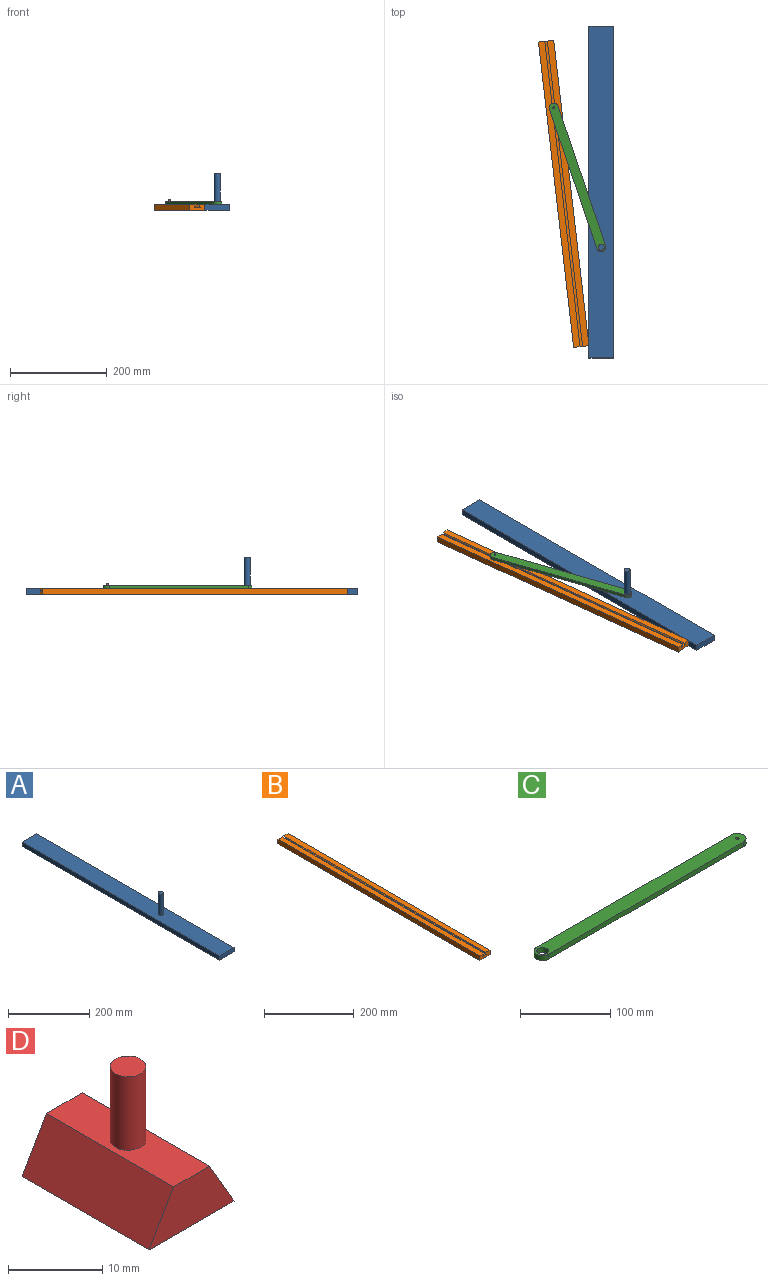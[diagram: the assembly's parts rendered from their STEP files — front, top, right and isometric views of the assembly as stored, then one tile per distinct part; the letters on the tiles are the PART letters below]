
ASSEMBLY  parts=4 mates=3
PART A: 8 faces, bbox 50.8x685.8x76.2 mm
  f0: plane 685.8x12.7mm, normal (-1,0,0), area 8709.7mm2, adj f1,f3,f4,f5
  f1: plane 685.8x50.8mm, normal (0,0,1), area 34712mm2, adj f0,f2,f4,f5,f6
  f2: plane 685.8x12.7mm, normal (1,0,0), area 8709.7mm2, adj f1,f3,f4,f5
  f3: plane 685.8x50.8mm, normal (0,0,-1), area 34838.6mm2, adj f0,f2,f4,f5
  f4: plane 50.8x12.7mm, normal (0,1,0), area 645.2mm2, adj f0,f1,f2,f3
  f5: plane 50.8x12.7mm, normal (0,-1,0), area 645.2mm2, adj f0,f1,f2,f3
  f6: cylinder r=6.35mm len=63.5mm, axis (0,0,-1), area 2533.5mm2, adj f1,f7
  f7: plane 12.7x12.7mm, normal (0,0,1), area 126.7mm2, adj f6
PART B: 10 faces, bbox 31.8x635x12.7 mm
  f0: plane 635x13.19mm, normal (0,0,1), area 8376.4mm2, adj f1,f2,f4,f8
  f1: plane 31.75x12.7mm, normal (0,1,0), area 345.9mm2, adj f0,f3,f4,f5,f6,f7,f8,f9
  f2: plane 31.75x12.7mm, normal (0,-1,0), area 345.9mm2, adj f0,f3,f4,f5,f6,f7,f8,f9
  f3: plane 635x31.75mm, normal (0,0,-1), area 20161.3mm2, adj f1,f2,f4,f6
  f4: plane 635x12.7mm, normal (1,0,0), area 8064.5mm2, adj f0,f1,f2,f3
  f5: plane 635x13.19mm, normal (0,0,1), area 8376.4mm2, adj f1,f2,f6,f7
  f6: plane 635x12.7mm, normal (-1,0,0), area 8064.5mm2, adj f1,f2,f3,f5
  f7: plane 635x6.35mm, normal (0.87,0,-0.5), area 4656mm2, adj f1,f2,f5,f9
  f8: plane 635x6.35mm, normal (-0.87,0,-0.5), area 4656mm2, adj f0,f1,f2,f9
  f9: plane 635x12.7mm, normal (0,0,1), area 8064.5mm2, adj f1,f2,f7,f8
PART C: 8 faces, bbox 323.9x19.1x6.4 mm
  f0: plane 304.8x6.35mm, normal (0,1,0), area 1935.5mm2, adj f1,f4,f6,f7
  f1: cylinder r=9.53mm len=19.05mm, axis (0,0,-1), area 190mm2, adj f0,f2,f6,f7
  f2: plane 304.8x6.35mm, normal (0,-1,0), area 1935.5mm2, adj f1,f4,f6,f7
  f3: cylinder r=6.35mm len=12.7mm, axis (0,0,-1), area 253.4mm2, adj f6,f7
  f4: cylinder r=9.53mm len=19.05mm, axis (0,0,-1), area 190mm2, adj f0,f2,f6,f7
  f5: cylinder r=1.91mm len=6.35mm, axis (0,0,-1), area 76mm2, adj f6,f7
  f6: plane 323.85x19.05mm, normal (0,0,1), area 5953.4mm2, adj f0,f1,f2,f3,f4,f5
  f7: plane 323.85x19.05mm, normal (0,0,-1), area 5953.4mm2, adj f0,f1,f2,f3,f4,f5
PART D: 8 faces, bbox 12.7x19.1x15.9 mm
  f0: plane 19.05x12.7mm, normal (0,0,-1), area 241.9mm2, adj f1,f3,f4,f5
  f1: plane 19.05x6.35mm, normal (0.87,0,0.5), area 139.7mm2, adj f0,f2,f4,f5
  f2: plane 19.05x5.37mm, normal (0,0,1), area 90.9mm2, adj f1,f3,f4,f5,f6
  f3: plane 19.05x6.35mm, normal (-0.87,0,0.5), area 139.7mm2, adj f0,f2,f4,f5
  f4: plane 12.7x6.35mm, normal (0,1,0), area 57.4mm2, adj f0,f1,f2,f3
  f5: plane 12.7x6.35mm, normal (0,-1,0), area 57.4mm2, adj f0,f1,f2,f3
  f6: cylinder r=1.91mm len=9.53mm, axis (0,0,-1), area 114mm2, adj f2,f7
  f7: plane 3.81x3.81mm, normal (0,0,1), area 11.4mm2, adj f6
PLACE A at identity fixed
PLACE B rot(axis=(0,0,1),6.6deg) t=(0,0,0)mm
PLACE C rot(axis=(0,0,1),108.8deg) t=(25.4,203.2,12.7)mm
PLACE D rot(axis=(0,0,1),6.6deg) t=(-71.6,482.32,6.35)mm
MATE slider D.f4 <-> B.f1  axis (-0.11,0.99,0) through (-73.78,501.25,6.35)mm
MATE revolute C.f3 <-> A.f6  axis (0,0,-1) through (25.4,203.2,12.7)mm
MATE revolute C.f5 <-> D.f6  axis (0,0,-1) through (-72.69,491.79,12.7)mm
